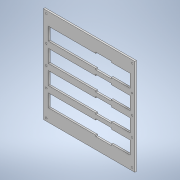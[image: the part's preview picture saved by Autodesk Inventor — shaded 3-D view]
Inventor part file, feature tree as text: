
AUTODESK INVENTOR PART (.ipt)
format: ipt  version: 2021 (Build 250183000, 183)  size: 200,704 bytes
history: native  units: mm
features: sketch x4, extrude x3, projected_geometry x2, pattern_linear x1, hole x1
ambient origin geometry x8: Origin, YZ Plane, XZ Plane, XY Plane, X Axis, Y Axis, Z Axis, Center Point
bodies: Solid1 (feature_tree)
feature tree (11):
  extrude  "Extrusion1"  Depth=110.0mm
  pattern_linear  "Rectangular Pattern1"  Count1=11  [1 undecoded]
  extrude  "Extrusion2"  Depth=82.0mm
  extrude  "Extrusion3"  Depth=40.4mm
  hole  "Hole1"  [1 undecoded]
  sketch  "Sketch1"  dims[d0=1.0mm d1=4.0mm d2=110.0mm]
  sketch  "Sketch2"  dims[d3=40.4mm d5=82.0mm]
  sketch  "Sketch3"  dims[d6=3.5mm d7=0.0mm d8=40.0mm d10=40.4mm]
  sketch  "Sketch4"  dims[d11=20.0mm d12=0.0mm d13=20.0mm d14=0.0mm d15=6.0mm d16=6.0mm d17=6.0mm d18=6.0mm d19=6.0mm d20=6.0mm d21=3.4mm d22=6.0mm d23=6.3mm d24=2.0mm d25=90.0deg d26=8.0mm d27=20.594885mm]
  projected_geometry  "Project Cut Edges1"
  projected_geometry  "Project Cut Edges2"
note: 2 required parameter values undecoded (feature->parameter linkage not recoverable at this tier; creation-order binding heuristic only, values carry confidence <= 0.55)
